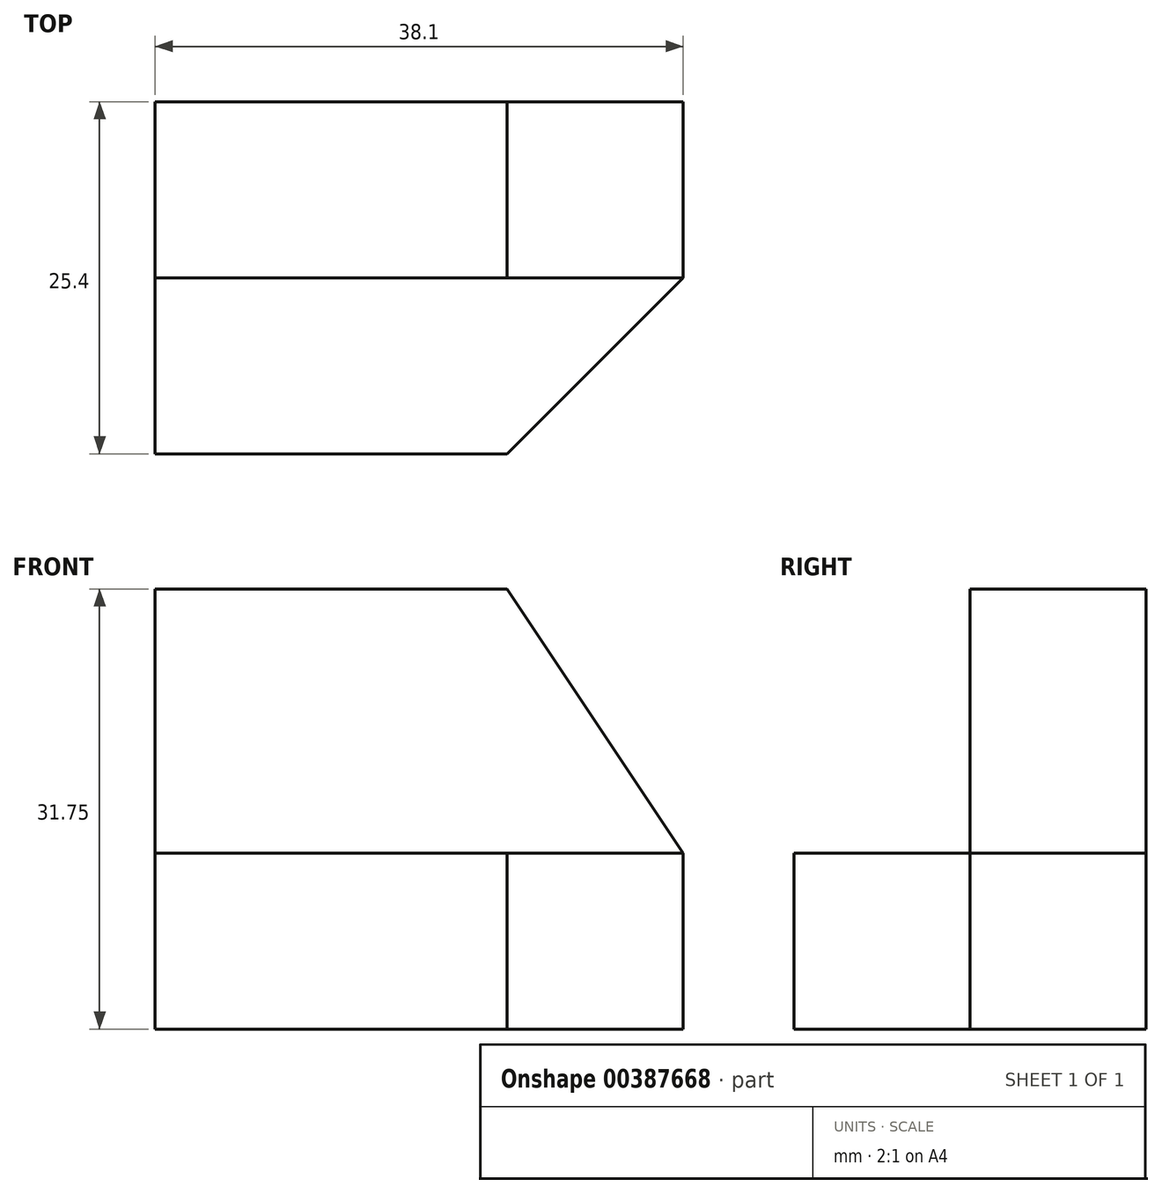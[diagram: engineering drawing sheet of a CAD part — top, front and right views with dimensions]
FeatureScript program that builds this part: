
annotation { "Feature Type Name" : "Feature", "Feature Type Description" : "" }
export const myFeature = defineFeature(function(context is Context, id is Id, definition is map)
    precondition{}
    {
        {
            var Q0;
            Q0=qCreatedBy(makeId("Right.planeOp"),FACE);
            var sketch = newSketch(context, id + "F0", { "sketchPlane" : qUnion([Q0])});
            skLineSegment(sketch, "E0", {"start": v(0, 0) * mm, "end": v(25.4, 0) * mm});
            skLineSegment(sketch, "E1", {"start": v(25.4, 0) * mm, "end": v(25.4, 31.75) * mm});
            skLineSegment(sketch, "E2", {"start": v(25.4, 31.75) * mm, "end": v(12.7, 31.75) * mm});
            skLineSegment(sketch, "E3", {"start": v(12.7, 31.75) * mm, "end": v(12.7, 12.7) * mm});
            skLineSegment(sketch, "E4", {"start": v(12.7, 12.7) * mm, "end": v(0, 12.7) * mm});
            skLineSegment(sketch, "E5", {"start": v(0, 12.7) * mm, "end": v(0, 0) * mm});
            skSolve(sketch);
        }
        {
            var Q0;
            Q0=makeQuery(id+"F0.imprint","IMPRINT",FACE,{"disambiguationData":[TD([[makeQuery(id+"F0.imprint","IMPRINT",EDGE,{"derivedFrom":sQuery(id+"F0.wireOp",EDGE,"E0")}),1.0]])]});
            extrude(context, id + "F1", {"entities" : qUnion([Q0]), "depth" : 38.1 * mm});
        }
        {
            var Q0;
            Q0=qCreatedBy(makeId("Top.planeOp"),FACE);
            var sketch = newSketch(context, id + "F2", { "sketchPlane" : qUnion([Q0])});
            skLineSegment(sketch, "E6", {"start": v(38.1, 0) * mm, "end": v(38.1, 12.7) * mm});
            skLineSegment(sketch, "E7", {"start": v(38.1, 12.7) * mm, "end": v(25.4, 0) * mm});
            skLineSegment(sketch, "E8", {"start": v(25.4, 0) * mm, "end": v(38.1, 0) * mm});
            skSolve(sketch);
        }
        {
            var Q0;
            Q0 = qSketchRegion(id + "F2", true);
            extrude(context, id + "F3", {"entities" : qUnion([Q0]), "operationType" : NewBodyOperationType.REMOVE, "depth" : 25.4 * mm});
        }
        {
            var Q0;
            Q0=makeQuery(id+"F1.opExtrude","SWEPT_FACE",FACE,{"disambiguationData":[OSD([sQuery(id+"F0.wireOp",EDGE,"E3")])]});
            var sketch = newSketch(context, id + "F4", { "sketchPlane" : qUnion([Q0])});
            skLineSegment(sketch, "E9", {"start": v(38.1, 12.7) * mm, "end": v(38.1, 31.75) * mm});
            skLineSegment(sketch, "E10", {"start": v(38.1, 31.75) * mm, "end": v(25.4, 31.75) * mm});
            skLineSegment(sketch, "E11", {"start": v(25.4, 31.75) * mm, "end": v(38.1, 12.7) * mm});
            skSolve(sketch);
        }
        {
            var Q0;
            Q0=makeQuery(id+"F4.imprint","IMPRINT",FACE,{"disambiguationData":[TD([[makeQuery(id+"F4.imprint","IMPRINT",EDGE,{"derivedFrom":sQuery(id+"F4.wireOp",EDGE,"E9")}),-1.0]])]});
            extrude(context, id + "F5", {"entities" : qUnion([Q0]), "operationType" : NewBodyOperationType.REMOVE, "oppositeDirection" : true, "depth" : 25.4 * mm});
        }
    });
